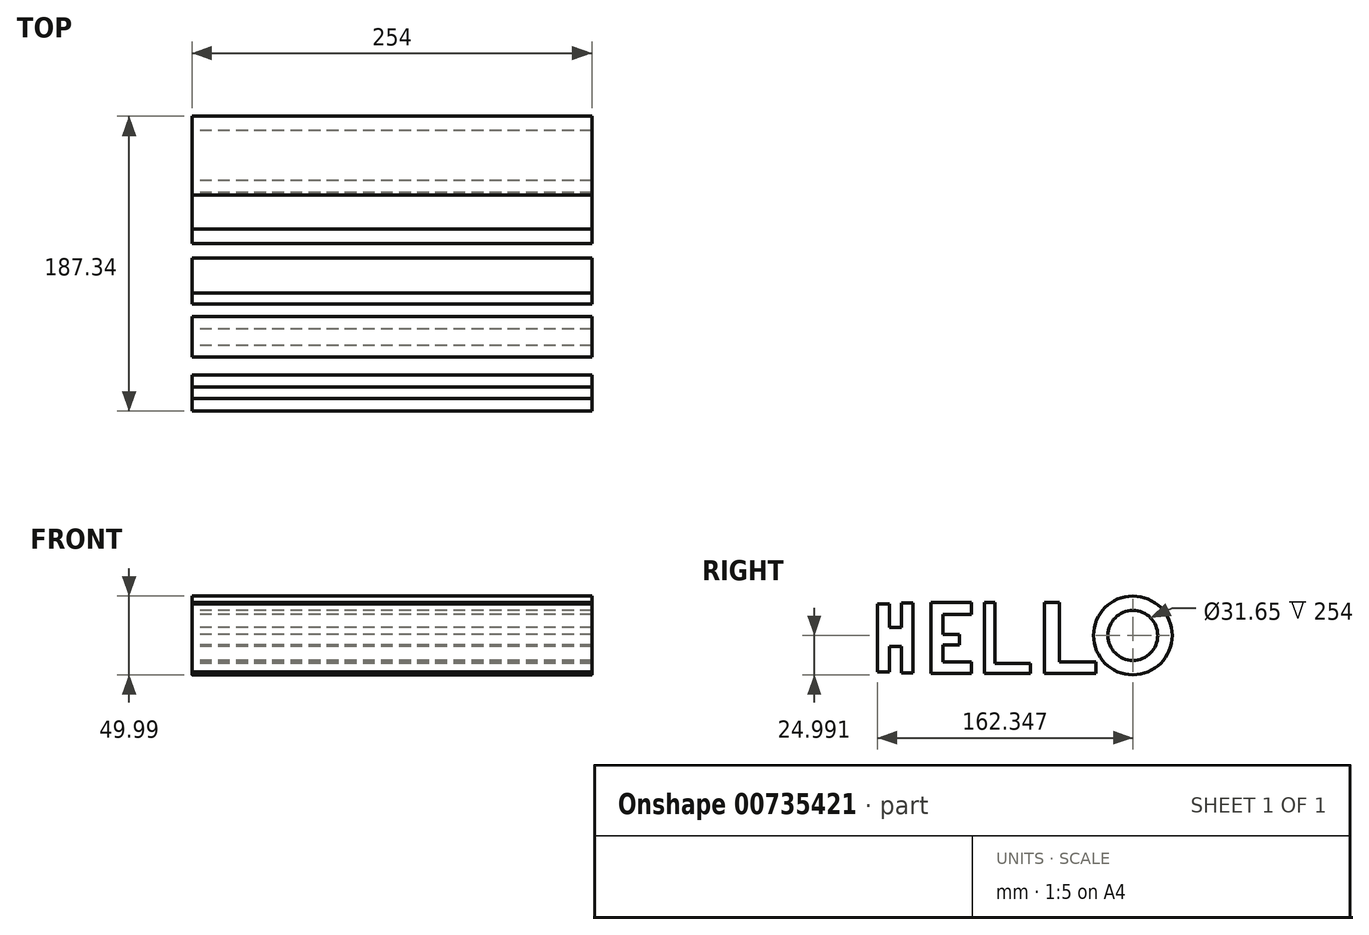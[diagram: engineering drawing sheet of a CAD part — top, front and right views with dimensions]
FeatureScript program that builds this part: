
annotation { "Feature Type Name" : "Feature", "Feature Type Description" : "" }
export const myFeature = defineFeature(function(context is Context, id is Id, definition is map)
    precondition{}
    {
        {
            var Q0;
            Q0=qCreatedBy(makeId("Right.planeOp"),FACE);
            var sketch = newSketch(context, id + "F0", { "sketchPlane" : qUnion([Q0])});
            skLineSegment(sketch, "E0.bottom", {"start": v(-86.64, -11.98) * mm, "end": v(-78.73, -11.98) * mm});
            skLineSegment(sketch, "E0.top", {"start": v(-86.64, 31.28) * mm, "end": v(-78.73, 31.28) * mm});
            skLineSegment(sketch, "E0.left", {"start": v(-86.64, -11.98) * mm, "end": v(-86.64, 31.28) * mm});
            skLineSegment(sketch, "E1.bottom", {"start": v(-71.29, 31.98) * mm, "end": v(-63.85, 31.98) * mm});
            skLineSegment(sketch, "E1.top", {"start": v(-71.29, -12.44) * mm, "end": v(-63.85, -12.44) * mm});
            skLineSegment(sketch, "E1.right", {"start": v(-63.85, 31.98) * mm, "end": v(-63.85, -12.44) * mm});
            skLineSegment(sketch, "E2.bottom", {"start": v(-71.29, 16.4) * mm, "end": v(-78.73, 16.4) * mm});
            skLineSegment(sketch, "E2.top", {"start": v(-71.29, 4.3) * mm, "end": v(-78.73, 4.3) * mm});
            skLineSegment(sketch, "E3.bottom", {"start": v(-52.45, 32.21) * mm, "end": v(-45, 32.21) * mm});
            skLineSegment(sketch, "E3.top", {"start": v(-52.45, -12.9) * mm, "end": v(-45, -12.9) * mm});
            skLineSegment(sketch, "E3.left", {"start": v(-52.45, 32.21) * mm, "end": v(-52.45, -12.9) * mm});
            skLineSegment(sketch, "E3.right", {"start": v(-45, 5.23) * mm, "end": v(-45, -5.7) * mm});
            skLineSegment(sketch, "E4.bottom", {"start": v(-45, 32.21) * mm, "end": v(-26.63, 32.21) * mm});
            skLineSegment(sketch, "E4.top", {"start": v(-45, 24.77) * mm, "end": v(-26.63, 24.77) * mm});
            skLineSegment(sketch, "E4.right", {"start": v(-26.63, 32.21) * mm, "end": v(-26.63, 24.77) * mm});
            skLineSegment(sketch, "E5.bottom", {"start": v(-45, -12.9) * mm, "end": v(-26.86, -12.9) * mm});
            skLineSegment(sketch, "E5.top", {"start": v(-45, -5.7) * mm, "end": v(-26.86, -5.7) * mm});
            skLineSegment(sketch, "E5.right", {"start": v(-26.86, -12.9) * mm, "end": v(-26.86, -5.7) * mm});
            skLineSegment(sketch, "E6.bottom", {"start": v(-45, 11.98) * mm, "end": v(-34.54, 11.98) * mm});
            skLineSegment(sketch, "E6.top", {"start": v(-45, 5.23) * mm, "end": v(-34.54, 5.23) * mm});
            skLineSegment(sketch, "E6.right", {"start": v(-34.54, 11.98) * mm, "end": v(-34.54, 5.23) * mm});
            skLineSegment(sketch, "E7.bottom", {"start": v(-18.5, 32.21) * mm, "end": v(-11.75, 32.21) * mm});
            skLineSegment(sketch, "E7.top", {"start": v(-18.5, -12.9) * mm, "end": v(-11.75, -12.9) * mm});
            skLineSegment(sketch, "E7.left", {"start": v(-18.5, 32.21) * mm, "end": v(-18.5, -12.9) * mm});
            skLineSegment(sketch, "E7.right", {"start": v(-11.75, 32.21) * mm, "end": v(-11.75, -6.4) * mm});
            skLineSegment(sketch, "E8.bottom", {"start": v(-11.75, -12.9) * mm, "end": v(10.58, -12.9) * mm});
            skLineSegment(sketch, "E8.top", {"start": v(-11.75, -6.4) * mm, "end": v(10.58, -6.4) * mm});
            skLineSegment(sketch, "E8.right", {"start": v(10.58, -12.9) * mm, "end": v(10.58, -6.4) * mm});
            skLineSegment(sketch, "E9.bottom", {"start": v(19.65, 32.21) * mm, "end": v(28.96, 32.21) * mm});
            skLineSegment(sketch, "E9.top", {"start": v(19.65, -12.9) * mm, "end": v(28.96, -12.9) * mm});
            skLineSegment(sketch, "E9.left", {"start": v(19.65, 32.21) * mm, "end": v(19.65, -12.9) * mm});
            skLineSegment(sketch, "E9.right", {"start": v(28.96, 32.21) * mm, "end": v(28.96, -5.7) * mm});
            skLineSegment(sketch, "E10.bottom", {"start": v(28.96, -12.9) * mm, "end": v(52.22, -12.9) * mm});
            skLineSegment(sketch, "E10.top", {"start": v(28.96, -5.7) * mm, "end": v(52.22, -5.7) * mm});
            skLineSegment(sketch, "E10.right", {"start": v(52.22, -12.9) * mm, "end": v(52.22, -5.7) * mm});
            skCircle(sketch, "E11", {"center": v(75.7, 11.28) * mm, "radius": 25 * mm});
            skCircle(sketch, "E12", {"center": v(75.7, 11.28) * mm, "radius": 15.82 * mm});
            skLineSegment(sketch, "E13.trimOffspring", {"start": v(-78.73, 16.4) * mm, "end": v(-78.73, 31.28) * mm});
            skLineSegment(sketch, "E14.trimOffspring", {"start": v(-71.29, 4.3) * mm, "end": v(-71.29, -12.44) * mm});
            skLineSegment(sketch, "E15", {"start": v(-45, 24.77) * mm, "end": v(-45, 11.98) * mm});
            skLineSegment(sketch, "E16", {"start": v(-71.29, 16.4) * mm, "end": v(-71.29, 31.98) * mm});
            skLineSegment(sketch, "E17", {"start": v(-78.73, -11.98) * mm, "end": v(-78.73, 4.3) * mm});
            skSolve(sketch);
        }
        {
            var Q0;
            Q0=makeQuery(id+"F0.imprint","IMPRINT",FACE,{"disambiguationData":[TD([[makeQuery(id+"F0.imprint","IMPRINT",EDGE,{"derivedFrom":sQuery(id+"F0.wireOp",EDGE,"E0.bottom")}),1.0]])]});
            var Q1;
            Q1=makeQuery(id+"F0.imprint","IMPRINT",FACE,{"disambiguationData":[TD([[makeQuery(id+"F0.imprint","IMPRINT",EDGE,{"derivedFrom":sQuery(id+"F0.wireOp",EDGE,"E3.bottom")}),-1.0]])]});
            var Q2;
            Q2=makeQuery(id+"F0.imprint","IMPRINT",FACE,{"disambiguationData":[TD([[makeQuery(id+"F0.imprint","IMPRINT",EDGE,{"derivedFrom":sQuery(id+"F0.wireOp",EDGE,"E7.bottom")}),-1.0]])]});
            var Q3;
            Q3=makeQuery(id+"F0.imprint","IMPRINT",FACE,{"disambiguationData":[TD([[makeQuery(id+"F0.imprint","IMPRINT",EDGE,{"derivedFrom":sQuery(id+"F0.wireOp",EDGE,"E9.bottom")}),-1.0]])]});
            var Q4;
            Q4=makeQuery(id+"F0.imprint","IMPRINT",FACE,{"disambiguationData":[TD([[makeQuery(id+"F0.imprint","IMPRINT",EDGE,{"derivedFrom":sQuery(id+"F0.wireOp",EDGE,"E11")}),1.0]])]});
            extrude(context, id + "F1", {"entities" : qUnion([Q0, Q1, Q2, Q3, Q4]), "depth" : 254 * mm, "offsetDistance" : 25.4 * mm});
        }
    });
